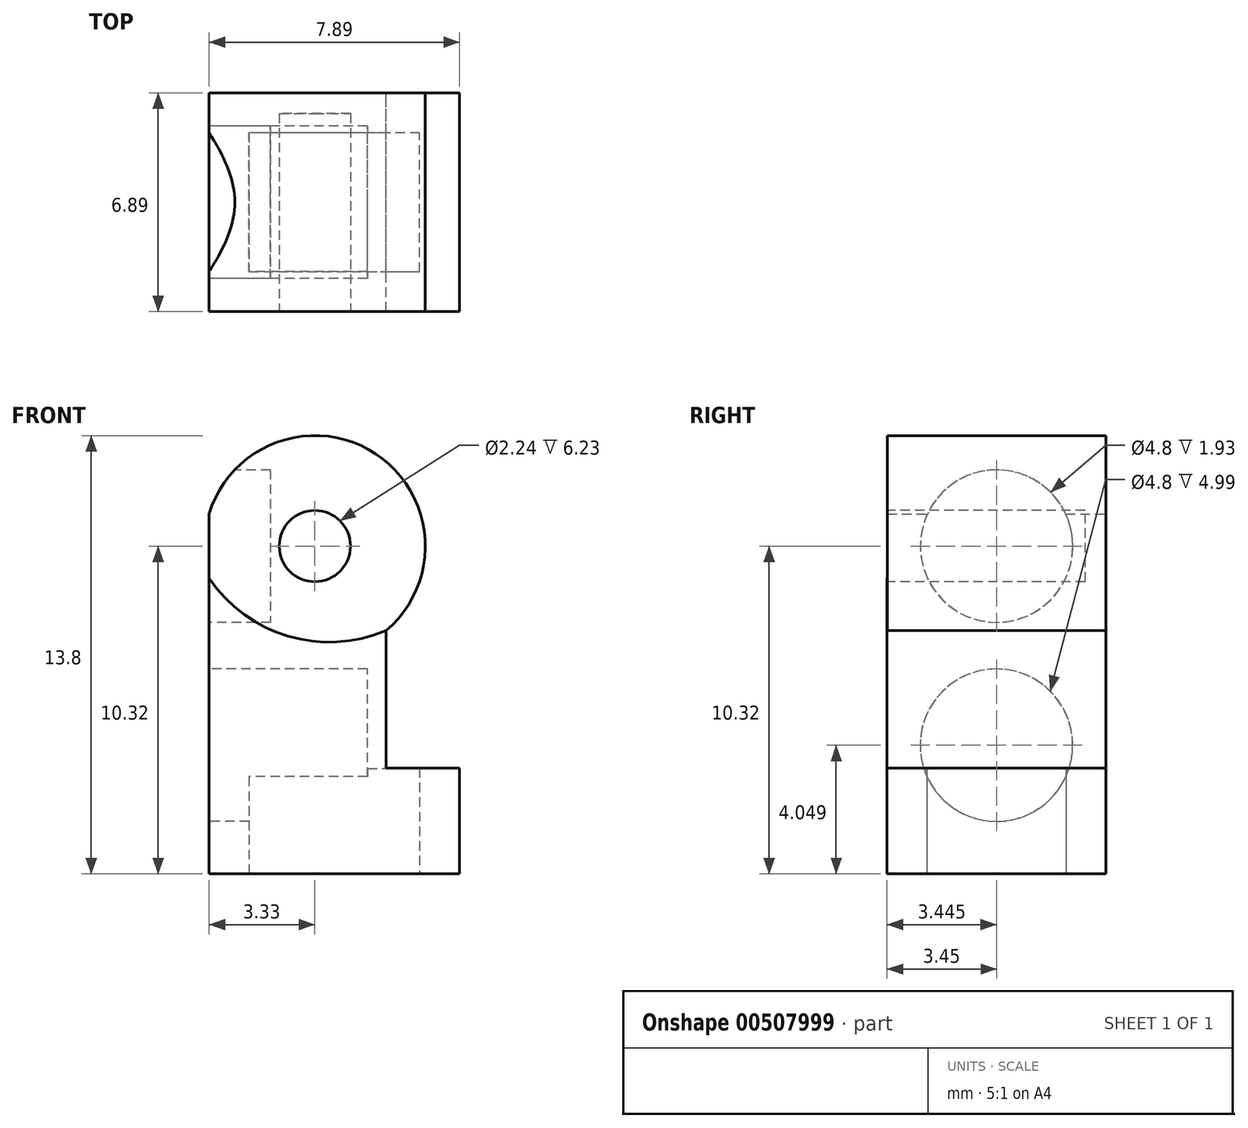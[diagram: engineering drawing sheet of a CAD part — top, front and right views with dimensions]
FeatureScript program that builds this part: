
annotation { "Feature Type Name" : "Feature", "Feature Type Description" : "" }
export const myFeature = defineFeature(function(context is Context, id is Id, definition is map)
    precondition{}
    {
        {
            var Q0;
            Q0=qCreatedBy(makeId("Front.planeOp"),FACE);
            var sketch = newSketch(context, id + "F0", { "sketchPlane" : qUnion([Q0])});
            skCircle(sketch, "E0", {"center": v(0, 0) * mm, "radius": 3.48 * mm});
            skSolve(sketch);
        }
        {
            var Q0;
            Q0 = qSketchRegion(id + "F0", true);
            extrude(context, id + "F1", {"entities" : qUnion([Q0]), "depth" : 6.88 * mm, "offsetDistance" : 25 * mm});
        }
        {
            var Q0;
            Q0=makeQuery(id+"F1.opExtrude","CAP_FACE",FACE,{"disambiguationData":[OSD([sQuery(id+"F0.wireOp",EDGE,"E0")])],"isStart":true});
            var sketch = newSketch(context, id + "F2", { "sketchPlane" : qUnion([Q0])});
            skLineSegment(sketch, "E1", {"start": v(3.33, 4.12) * mm, "end": v(3.33, -5.88) * mm});
            skLineSegment(sketch, "E2", {"start": v(3.33, 4.12) * mm, "end": v(4.84, 2.14) * mm});
            skLineSegment(sketch, "E3", {"start": v(4.84, 2.14) * mm, "end": v(3.33, -5.88) * mm});
            skSolve(sketch);
        }
        {
            var Q0;
            Q0 = qSketchRegion(id + "F2", true);
            extrude(context, id + "F3", {"entities" : qUnion([Q0]), "operationType" : NewBodyOperationType.REMOVE, "endBound" : BoundingType.THROUGH_ALL, "oppositeDirection" : true, "depth" : 25 * mm, "offsetDistance" : 25 * mm});
        }
        {
            var Q0;
            Q0=makeQuery(id+"F1.opExtrude","CAP_FACE",FACE,{"disambiguationData":[OSD([sQuery(id+"F0.wireOp",EDGE,"E0")])],"isStart":true});
            var sketch = newSketch(context, id + "F4", { "sketchPlane" : qUnion([Q0])});
            skLineSegment(sketch, "E4", {"start": v(3.33, -1.01) * mm, "end": v(3.33, -10.32) * mm});
            skLineSegment(sketch, "E5", {"start": v(3.33, -10.32) * mm, "end": v(-4.56, -10.32) * mm});
            skLineSegment(sketch, "E6", {"start": v(-4.56, -10.32) * mm, "end": v(-4.56, -7) * mm});
            skLineSegment(sketch, "E7", {"start": v(-4.56, -7) * mm, "end": v(-2.24, -7) * mm});
            skLineSegment(sketch, "E8", {"start": v(-2.24, -7) * mm, "end": v(-2.24, -2.66) * mm});
            skArc(sketch, "E9", {"start": v(-2.24, -2.66) * mm, "mid": v(0.84, -2.84) * mm, "end": v(3.33, -1.01) * mm});
            skSolve(sketch);
        }
        {
            var Q0;
            Q0 = qSketchRegion(id + "F4", true);
            extrude(context, id + "F5", {"entities" : qUnion([Q0]), "operationType" : NewBodyOperationType.ADD, "oppositeDirection" : true, "depth" : 6.9 * mm, "offsetDistance" : 25 * mm});
        }
        {
            var Q0;
            Q0=makeQuery(id+"F5.opExtrude","SWEPT_FACE",FACE,{"disambiguationData":[OSD([sQuery(id+"F4.wireOp",EDGE,"E5")])]});
            var sketch = newSketch(context, id + "F6", { "sketchPlane" : qUnion([Q0])});
            skLineSegment(sketch, "E10", {"start": v(-2.07, 1.26) * mm, "end": v(-2.07, 5.63) * mm});
            skLineSegment(sketch, "E11", {"start": v(3.3, 1.26) * mm, "end": v(3.3, 5.63) * mm});
            skLineSegment(sketch, "E12", {"start": v(3.3, 1.26) * mm, "end": v(-2.07, 1.26) * mm});
            skLineSegment(sketch, "E13", {"start": v(-2.07, 5.63) * mm, "end": v(3.3, 5.63) * mm});
            skSolve(sketch);
        }
        {
            var Q0;
            Q0 = qSketchRegion(id + "F6", true);
            extrude(context, id + "F7", {"entities" : qUnion([Q0]), "operationType" : NewBodyOperationType.REMOVE, "oppositeDirection" : true, "depth" : 3.32 * mm, "offsetDistance" : 25 * mm});
        }
        {
            var Q0;
            Q0=makeQuery(id+"F5.boolean.opBoolean","MERGE",FACE,{"derivedFrom":[makeQuery(id+"F3.boolean.opBoolean","COPY",FACE,{"derivedFrom":makeQuery(id+"F3.opExtrude","SWEPT_FACE",FACE,{"disambiguationData":[OSD([sQuery(id+"F2.wireOp",EDGE,"E1")])]})}),makeQuery(id+"F5.opExtrude","SWEPT_FACE",FACE,{"disambiguationData":[OSD([sQuery(id+"F4.wireOp",EDGE,"E4")])]})]});
            var sketch = newSketch(context, id + "F8", { "sketchPlane" : qUnion([Q0])});
            skCircle(sketch, "E14", {"center": v(3.44, 0) * mm, "radius": 2.4 * mm});
            skPoint(sketch, "E14.centerSnap0", {"position": v(3.44, 1.01) * mm});
            skPoint(sketch, "E14.centerSnap1", {"position": v(6.88, 0) * mm});
            skSolve(sketch);
        }
        {
            var Q0;
            Q0 = qSketchRegion(id + "F8", true);
            extrude(context, id + "F9", {"entities" : qUnion([Q0]), "operationType" : NewBodyOperationType.REMOVE, "oppositeDirection" : true, "depth" : 1.93 * mm, "offsetDistance" : 25 * mm});
        }
        {
            var Q0;
            Q0=makeQuery(id+"F5.boolean.opBoolean","MERGE",FACE,{"derivedFrom":[makeQuery(id+"F3.boolean.opBoolean","COPY",FACE,{"derivedFrom":makeQuery(id+"F3.opExtrude","SWEPT_FACE",FACE,{"disambiguationData":[OSD([sQuery(id+"F2.wireOp",EDGE,"E1")])]})}),makeQuery(id+"F5.opExtrude","SWEPT_FACE",FACE,{"disambiguationData":[OSD([sQuery(id+"F4.wireOp",EDGE,"E4")])]})]});
            var sketch = newSketch(context, id + "F10", { "sketchPlane" : qUnion([Q0])});
            skCircle(sketch, "E15", {"center": v(3.45, -6.27) * mm, "radius": 2.4 * mm});
            skPoint(sketch, "E15.centerSnap0", {"position": v(3.45, -10.32) * mm});
            skSolve(sketch);
        }
        {
            var Q0;
            Q0 = qSketchRegion(id + "F10", true);
            extrude(context, id + "F11", {"entities" : qUnion([Q0]), "operationType" : NewBodyOperationType.REMOVE, "oppositeDirection" : true, "depth" : 5 * mm, "offsetDistance" : 25 * mm});
        }
        {
            var Q0;
            Q0=makeQuery(id+"F1.opExtrude","CAP_FACE",FACE,{"disambiguationData":[OSD([sQuery(id+"F0.wireOp",EDGE,"E0")])],"isStart":false});
            var sketch = newSketch(context, id + "F12", { "sketchPlane" : qUnion([Q0])});
            skCircle(sketch, "E16", {"center": v(0, 0) * mm, "radius": 1.12 * mm});
            skSolve(sketch);
        }
        {
            var Q0;
            Q0 = qSketchRegion(id + "F12", true);
            extrude(context, id + "F13", {"entities" : qUnion([Q0]), "operationType" : NewBodyOperationType.REMOVE, "oppositeDirection" : true, "depth" : 6.23 * mm, "offsetDistance" : 25 * mm});
        }
    });
